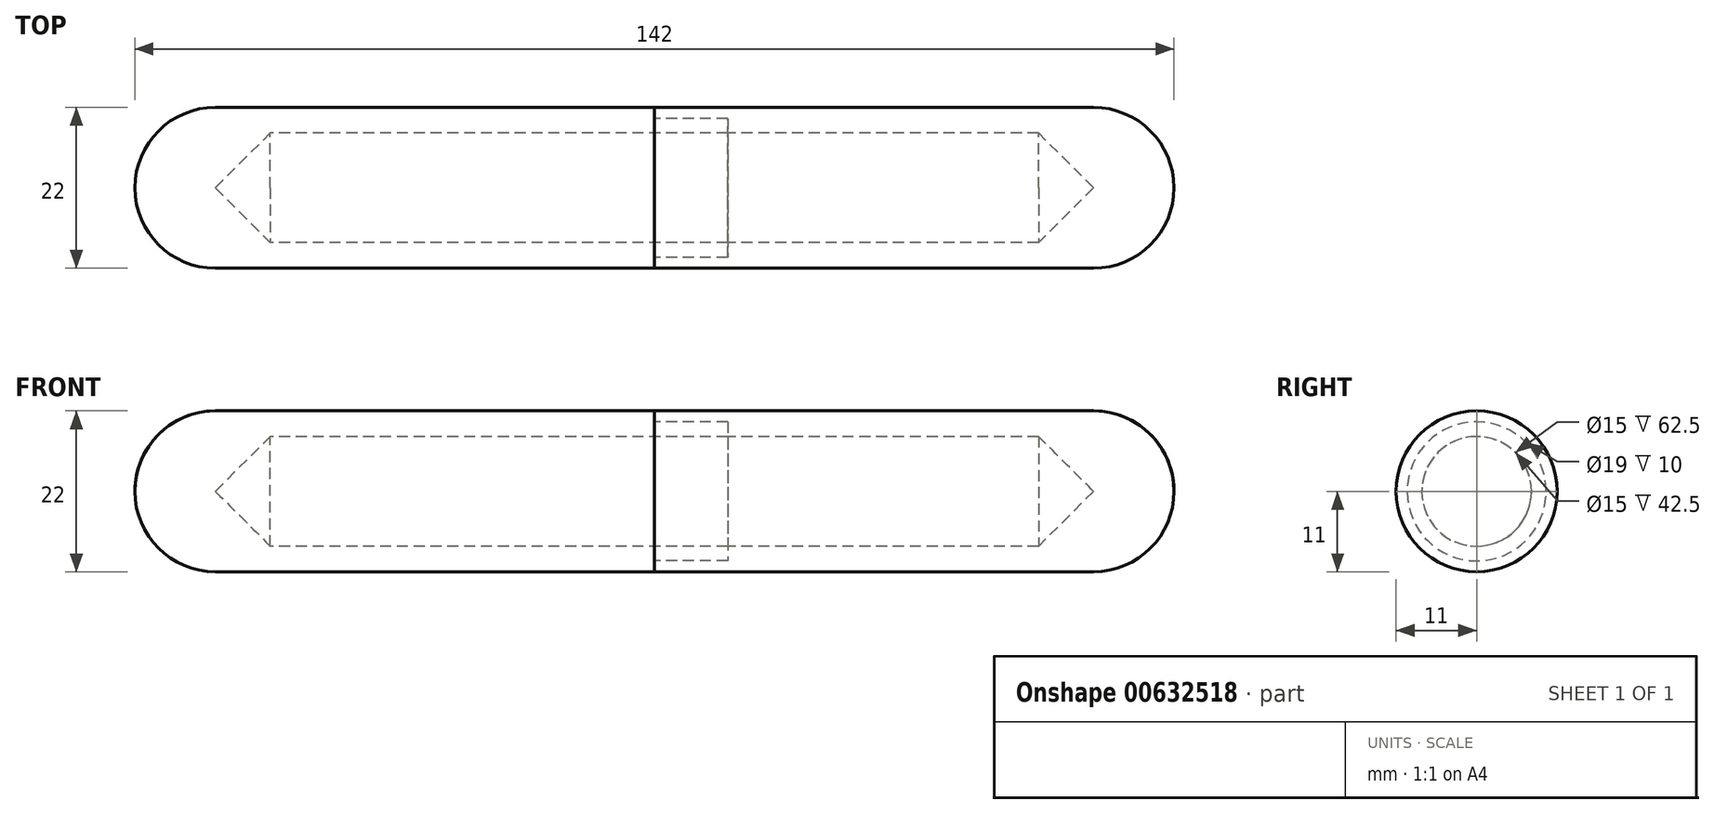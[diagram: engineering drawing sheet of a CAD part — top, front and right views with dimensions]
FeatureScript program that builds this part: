
annotation { "Feature Type Name" : "Feature", "Feature Type Description" : "" }
export const myFeature = defineFeature(function(context is Context, id is Id, definition is map)
    precondition{}
    {
        {
            var Q0;
            Q0=qCreatedBy(makeId("Front.planeOp"),FACE);
            var sketch = newSketch(context, id + "F0", { "sketchPlane" : qUnion([Q0])});
            skLineSegment(sketch, "E0", {"start": v(0, 0) * mm, "end": v(0, 7.5) * mm, "construction": true});
            skLineSegment(sketch, "E1", {"start": v(0, 7.5) * mm, "end": v(10, 7.5) * mm});
            skLineSegment(sketch, "E2", {"start": v(10, 7.5) * mm, "end": v(10, 9.5) * mm});
            skLineSegment(sketch, "E3", {"start": v(10, 9.5) * mm, "end": v(0, 9.5) * mm});
            skLineSegment(sketch, "E4", {"start": v(0, 9.5) * mm, "end": v(0, 11) * mm});
            skLineSegment(sketch, "E5", {"start": v(0, 11) * mm, "end": v(-60, 11) * mm});
            skLineSegment(sketch, "E6", {"start": v(-60, 11) * mm, "end": v(-60, 0) * mm});
            skLineSegment(sketch, "E7", {"start": v(-60, 0) * mm, "end": v(0, 0) * mm, "construction": true});
            skLineSegment(sketch, "E8", {"start": v(0, 7.5) * mm, "end": v(-60, 7.5) * mm});
            skArc(sketch, "E9", {"start": v(-60, 11) * mm, "mid": v(-67.78, 7.78) * mm, "end": v(-71, 0) * mm});
            skLineSegment(sketch, "E10", {"start": v(0, 11) * mm, "end": v(60, 11) * mm});
            skArc(sketch, "E11", {"start": v(60, 11) * mm, "mid": v(67.78, 7.78) * mm, "end": v(71, 0) * mm});
            skLineSegment(sketch, "E12", {"start": v(10, 7.5) * mm, "end": v(60, 7.5) * mm});
            skLineSegment(sketch, "E13", {"start": v(60, 7.5) * mm, "end": v(60, 0) * mm});
            skLineSegment(sketch, "E14", {"start": v(-71, 0) * mm, "end": v(-60, 0) * mm});
            skLineSegment(sketch, "E15", {"start": v(60, 0) * mm, "end": v(71, 0) * mm});
            skSolve(sketch);
        }
        {
            var Q0;
            Q0=makeQuery(id+"F0.imprint","IMPRINT",FACE,{"disambiguationData":[TD([[makeQuery(id+"F0.imprint","IMPRINT",EDGE,{"derivedFrom":sQuery(id+"F0.wireOp",EDGE,"E2")}),-1.0]])]});
            var Q1;
            Q1=sQuery(id+"F0.wireOp",EDGE,"E7");
            revolve(context, id + "F1", {"entities" : qUnion([Q0]), "axis" : qUnion([Q1]), "revolveType" : RevolveType.FULL});
        }
        {
            var Q0;
            Q0=makeQuery(id+"F0.imprint","IMPRINT",FACE,{"disambiguationData":[TD([[makeQuery(id+"F0.imprint","IMPRINT",EDGE,{"derivedFrom":sQuery(id+"F0.wireOp",EDGE,"E1")}),1.0]])]});
            var Q1;
            {var subQ0=sQuery(id+"F0.wireOp",EDGE,"E9");Q1=makeQuery(id+"F0.imprint","IMPRINT",FACE,{"disambiguationData":[TD([[makeQuery(id+"F0.imprint","IMPRINT",EDGE,{"derivedFrom":subQ0}),1.0]])]});}
            var Q2;
            Q2=sQuery(id+"F0.wireOp",EDGE,"E7");
            revolve(context, id + "F2", {"entities" : qUnion([Q0, Q1]), "axis" : qUnion([Q2]), "revolveType" : RevolveType.FULL});
        }
        {
            var Q0;
            Q0=makeQuery(id+"F2.opRevolve","SWEPT_EDGE",EDGE,{"disambiguationData":[OSD([sQuery(id+"F0.wireOp",EDGE,"E6"),sQuery(id+"F0.wireOp",EDGE,"E8")])]});
            chamfer(context, id + "F3", {"entities" : qUnion([Q0]), "width" : 7.5 * mm, "tangentPropagation" : true});
        }
        {
            var Q0;
            Q0=makeQuery(id+"F1.opRevolve","SWEPT_EDGE",EDGE,{"disambiguationData":[OSD([sQuery(id+"F0.wireOp",EDGE,"E12"),sQuery(id+"F0.wireOp",EDGE,"E13")])]});
            chamfer(context, id + "F4", {"entities" : qUnion([Q0]), "width" : 7.5 * mm, "tangentPropagation" : true});
        }
    });
